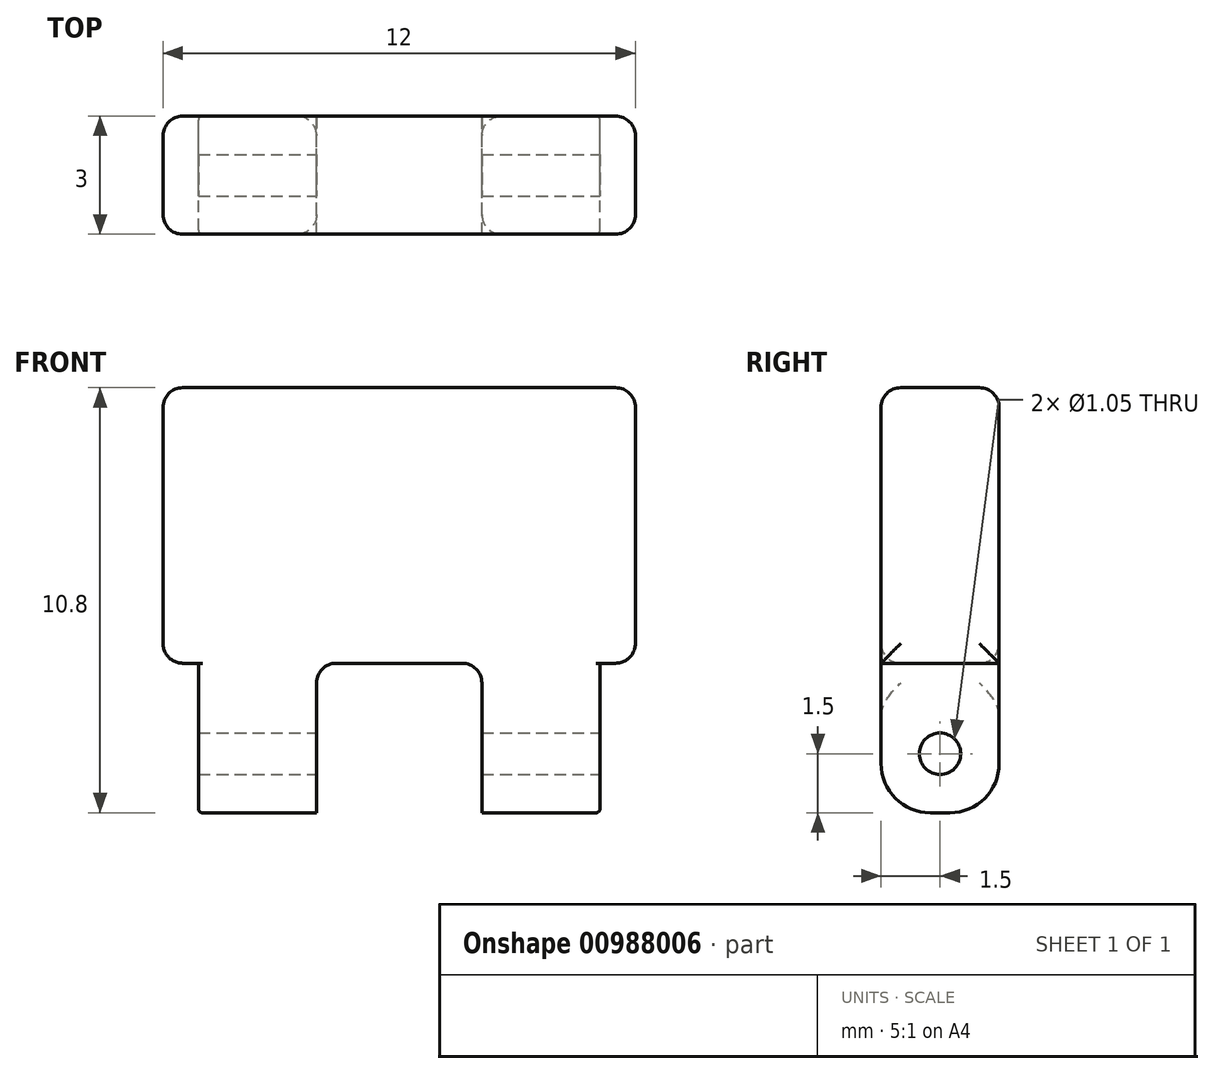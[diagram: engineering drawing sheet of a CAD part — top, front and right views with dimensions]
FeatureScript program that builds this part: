
annotation { "Feature Type Name" : "Feature", "Feature Type Description" : "" }
export const myFeature = defineFeature(function(context is Context, id is Id, definition is map)
    precondition{}
    {
        {
            var Q0;
            Q0=qCreatedBy(makeId("Front.planeOp"),FACE);
            var sketch = newSketch(context, id + "F0", { "sketchPlane" : qUnion([Q0])});
            skLineSegment(sketch, "E0.bottom", {"start": v(6, 3.5) * mm, "end": v(-6, 3.5) * mm});
            skLineSegment(sketch, "E0.top", {"start": v(6, -3.5) * mm, "end": v(-6, -3.5) * mm});
            skLineSegment(sketch, "E0.left", {"start": v(6, 3.5) * mm, "end": v(6, -3.5) * mm});
            skLineSegment(sketch, "E0.right", {"start": v(-6, 3.5) * mm, "end": v(-6, -3.5) * mm});
            skPoint(sketch, "E0.middle", {"position": v(0, 0) * mm});
            skLineSegment(sketch, "E1", {"start": v(0, 3.5) * mm, "end": v(0, -3.5) * mm});
            skLineSegment(sketch, "E2.bottom", {"start": v(-5.1, -3.5) * mm, "end": v(-2.1, -3.5) * mm});
            skLineSegment(sketch, "E2.top", {"start": v(-5.1, -7.3) * mm, "end": v(-2.1, -7.3) * mm});
            skLineSegment(sketch, "E2.left", {"start": v(-5.1, -3.5) * mm, "end": v(-5.1, -7.3) * mm});
            skLineSegment(sketch, "E2.right", {"start": v(-2.1, -3.5) * mm, "end": v(-2.1, -7.3) * mm});
            skLineSegment(sketch, "E3.MirrorCS", {"start": v(5.1, -3.5) * mm, "end": v(5.1, -7.3) * mm});
            skLineSegment(sketch, "E4.MirrorCS", {"start": v(5.1, -7.3) * mm, "end": v(2.1, -7.3) * mm});
            skLineSegment(sketch, "E5.MirrorCS", {"start": v(5.1, -3.5) * mm, "end": v(2.1, -3.5) * mm});
            skLineSegment(sketch, "E6.MirrorCS", {"start": v(2.1, -3.5) * mm, "end": v(2.1, -7.3) * mm});
            skSolve(sketch);
        }
        {
            var Q0;
            {var subQ12=sQuery(id+"F0.wireOp",EDGE,"E0.right");var subQ14=sQuery(id+"F0.wireOp",EDGE,"E3.MirrorCS");var subQ19=sQuery(id+"F0.wireOp",EDGE,"E0.left");Q0=qUnion([makeQuery(id+"F0.imprint","IMPRINT",FACE,{"disambiguationData":[TD([[makeQuery(id+"F0.imprint","IMPRINT",EDGE,{"derivedFrom":subQ19}),-1.0]])]}),makeQuery(id+"F0.imprint","IMPRINT",FACE,{"disambiguationData":[TD([[makeQuery(id+"F0.imprint","IMPRINT",EDGE,{"derivedFrom":subQ14}),-1.0]])]}),makeQuery(id+"F0.imprint","IMPRINT",FACE,{"disambiguationData":[TD([[makeQuery(id+"F0.imprint","IMPRINT",EDGE,{"derivedFrom":sQuery(id+"F0.wireOp",EDGE,"E2.top")}),1.0]])]}),makeQuery(id+"F0.imprint","IMPRINT",FACE,{"disambiguationData":[TD([[makeQuery(id+"F0.imprint","IMPRINT",EDGE,{"derivedFrom":subQ12}),1.0]])]})]);}
            extrude(context, id + "F1", {"entities" : qUnion([Q0]), "depth" : 3 * mm, "offsetDistance" : 25 * mm});
        }
        {
            var Q0;
            Q0=makeQuery(id+"F1.opExtrude","SWEPT_FACE",FACE,{"disambiguationData":[OSD([sQuery(id+"F0.wireOp",EDGE,"E3.MirrorCS")])]});
            var sketch = newSketch(context, id + "F2", { "sketchPlane" : qUnion([Q0])});
            skLineSegment(sketch, "E7", {"start": v(-1.5, -7.3) * mm, "end": v(-1.5, -3.5) * mm});
            skCircle(sketch, "E8", {"center": v(-1.5, -5.8) * mm, "radius": 0.53 * mm});
            skSolve(sketch);
        }
        {
            var Q0;
            Q0 = qSketchRegion(id + "F2", true);
            extrude(context, id + "F3", {"entities" : qUnion([Q0]), "operationType" : NewBodyOperationType.REMOVE, "endBound" : BoundingType.THROUGH_ALL, "oppositeDirection" : true, "depth" : 25 * mm, "offsetDistance" : 25 * mm});
        }
        {
            var Q0;
            Q0=makeQuery(id+"F1.opExtrude","CAP_EDGE",EDGE,{"disambiguationData":[OSD([sQuery(id+"F0.wireOp",EDGE,"E2.top")])],"isStart":false});
            var Q1;
            Q1=makeQuery(id+"F1.opExtrude","CAP_EDGE",EDGE,{"disambiguationData":[OSD([sQuery(id+"F0.wireOp",EDGE,"E2.top")])],"isStart":true});
            var Q2;
            Q2=makeQuery(id+"F1.opExtrude","CAP_EDGE",EDGE,{"disambiguationData":[OSD([sQuery(id+"F0.wireOp",EDGE,"E4.MirrorCS")])],"isStart":false});
            var Q3;
            Q3=makeQuery(id+"F1.opExtrude","CAP_EDGE",EDGE,{"disambiguationData":[OSD([sQuery(id+"F0.wireOp",EDGE,"E4.MirrorCS")])],"isStart":true});
            fillet(context, id + "F4", {"entities" : qUnion([Q0, Q1, Q2, Q3]), "radius" : 1.25 * mm, "tangentPropagation" : true, "allowEdgeOverflow" : false});
        }
        {
            var Q0;
            {var subQ0=sQuery(id+"F0.wireOp",EDGE,"E0.top");var subQ1=makeQuery(id+"F0.imprint","INTERSECT",VERTEX,{"derivedFrom":[subQ0,sQuery(id+"F0.wireOp",EDGE,"E1")]});Q0=makeQuery(id+"F1.opExtrude","SWEPT_FACE",FACE,{"disambiguationData":[OSD([subQ0]),TDD([makeQuery(id+"F0.imprint","IMPRINT",EDGE,{"disambiguationData":[TD([[subQ1,1.0]])],"derivedFrom":subQ0}),makeQuery(id+"F0.imprint","IMPRINT",EDGE,{"disambiguationData":[TD([[subQ1,-1.0]])],"derivedFrom":subQ0})])]});}
            var Q1;
            Q1=makeQuery(id+"F1.opExtrude","SWEPT_FACE",FACE,{"disambiguationData":[OSD([sQuery(id+"F0.wireOp",EDGE,"E0.right")])]});
            var Q2;
            Q2=makeQuery(id+"F1.opExtrude","SWEPT_FACE",FACE,{"disambiguationData":[OSD([sQuery(id+"F0.wireOp",EDGE,"E0.left")])]});
            var Q3;
            Q3=makeQuery(id+"F1.opExtrude","SWEPT_FACE",FACE,{"disambiguationData":[OSD([sQuery(id+"F0.wireOp",EDGE,"E0.bottom")])]});
            fillet(context, id + "F5", {"entities" : qUnion([Q0, Q1, Q2, Q3]), "radius" : .5 * mm, "tangentPropagation" : true, "allowEdgeOverflow" : false});
        }
        {
            var Q0;
            Q0=makeQuery(id+"F4.opFillet","BLEND_EDGE",EDGE,{"blendedFrom":[makeQuery(id+"F1.opExtrude","CAP_EDGE",EDGE,{"disambiguationData":[OSD([sQuery(id+"F0.wireOp",EDGE,"E2.top")])],"isStart":false}),makeQuery(id+"F1.opExtrude","SWEPT_FACE",FACE,{"disambiguationData":[OSD([sQuery(id+"F0.wireOp",EDGE,"E2.left")])]})],"blendedInto":[makeQuery(id+"F1.opExtrude","SWEPT_FACE",FACE,{"disambiguationData":[OSD([sQuery(id+"F0.wireOp",EDGE,"E2.left")])]})]});
            var Q1;
            Q1=makeQuery(id+"F1.opExtrude","CAP_EDGE",EDGE,{"disambiguationData":[OSD([sQuery(id+"F0.wireOp",EDGE,"E3.MirrorCS")])],"isStart":false});
            fillet(context, id + "F6", {"entities" : qUnion([Q0, Q1]), "radius" : .1 * mm, "tangentPropagation" : true, "allowEdgeOverflow" : false});
        }
    });
